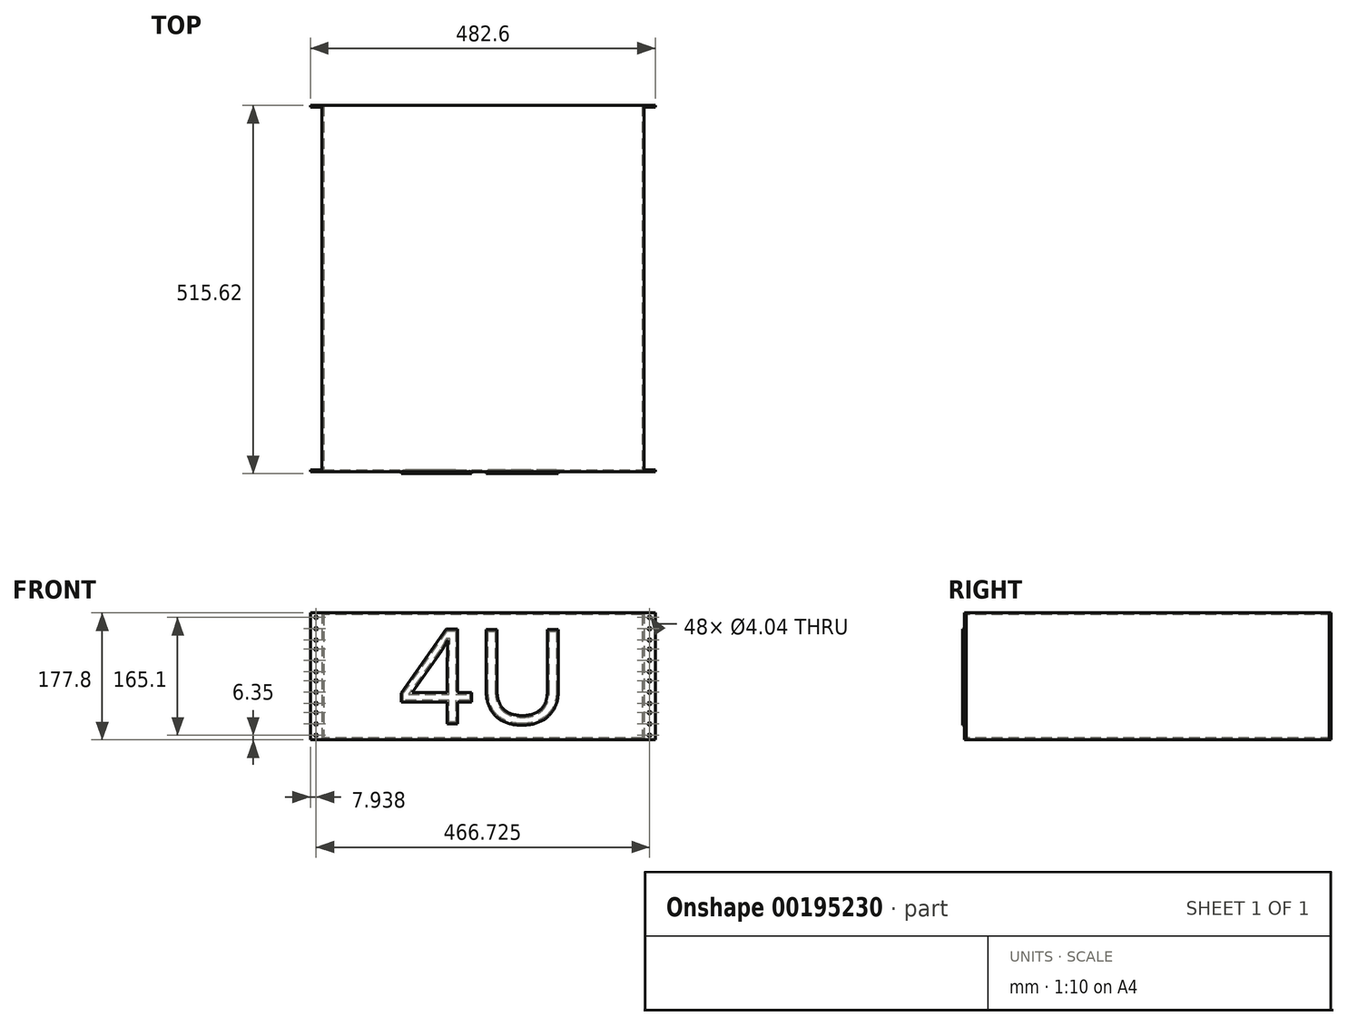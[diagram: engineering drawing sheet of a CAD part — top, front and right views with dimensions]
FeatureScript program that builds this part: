
annotation { "Feature Type Name" : "Feature", "Feature Type Description" : "" }
export const myFeature = defineFeature(function(context is Context, id is Id, definition is map)
    precondition{}
    {
        {
            var Q0;
            Q0=qCreatedBy(makeId("Front.planeOp"),FACE);
            var sketch = newSketch(context, id + "F0", { "sketchPlane" : qUnion([Q0])});
            skLineSegment(sketch, "E0.bottom", {"start": v(-241.3, 88.9) * mm, "end": v(241.3, 88.9) * mm});
            skLineSegment(sketch, "E0.top", {"start": v(-241.3, -88.9) * mm, "end": v(241.3, -88.9) * mm});
            skLineSegment(sketch, "E0.left", {"start": v(-241.3, 88.9) * mm, "end": v(-241.3, -88.9) * mm});
            skLineSegment(sketch, "E0.right", {"start": v(241.3, 88.9) * mm, "end": v(241.3, -88.9) * mm});
            skPoint(sketch, "E0.middle", {"position": v(0, 0) * mm});
            skSolve(sketch);
        }
        {
            var Q0;
            Q0 = qSketchRegion(id + "F0", true);
            extrude(context, id + "F1", {"entities" : qUnion([Q0]), "depth" : 2.54 * mm});
        }
        {
            var Q0;
            Q0=makeQuery(id+"F1.opExtrude","CAP_FACE",FACE,{"disambiguationData":[OSD([sQuery(id+"F0.wireOp",EDGE,"E0.bottom"),sQuery(id+"F0.wireOp",EDGE,"E0.top"),sQuery(id+"F0.wireOp",EDGE,"E0.left"),sQuery(id+"F0.wireOp",EDGE,"E0.right")])],"isStart":true});
            var sketch = newSketch(context, id + "F2", { "sketchPlane" : qUnion([Q0])});
            skLineSegment(sketch, "E1.bottom", {"start": v(-225.42, 88.9) * mm, "end": v(225.42, 88.9) * mm});
            skLineSegment(sketch, "E1.top", {"start": v(-225.42, -88.9) * mm, "end": v(225.42, -88.9) * mm});
            skLineSegment(sketch, "E1.left", {"start": v(-225.42, 88.9) * mm, "end": v(-225.42, -88.9) * mm});
            skLineSegment(sketch, "E1.right", {"start": v(225.42, 88.9) * mm, "end": v(225.42, -88.9) * mm});
            skPoint(sketch, "E1.middle", {"position": v(0, 0) * mm});
            skSolve(sketch);
        }
        {
            var Q0;
            Q0 = qSketchRegion(id + "F2", true);
            extrude(context, id + "F3", {"entities" : qUnion([Q0]), "operationType" : NewBodyOperationType.ADD, "depth" : 508 * mm});
        }
        {
            var Q0;
            Q0=makeQuery(id+"F3.opExtrude","CAP_FACE",FACE,{"disambiguationData":[OSD([sQuery(id+"F2.wireOp",EDGE,"E1.bottom"),sQuery(id+"F2.wireOp",EDGE,"E1.top"),sQuery(id+"F2.wireOp",EDGE,"E1.left"),sQuery(id+"F2.wireOp",EDGE,"E1.right")])],"isStart":false});
            var sketch = newSketch(context, id + "F4", { "sketchPlane" : qUnion([Q0])});
            skLineSegment(sketch, "E2.bottom", {"start": v(-241.3, 88.9) * mm, "end": v(241.3, 88.9) * mm});
            skLineSegment(sketch, "E2.top", {"start": v(-241.3, -88.9) * mm, "end": v(241.3, -88.9) * mm});
            skLineSegment(sketch, "E2.left", {"start": v(-241.3, 88.9) * mm, "end": v(-241.3, -88.9) * mm});
            skLineSegment(sketch, "E2.right", {"start": v(241.3, 88.9) * mm, "end": v(241.3, -88.9) * mm});
            skPoint(sketch, "E2.middle", {"position": v(0, 0) * mm});
            skSolve(sketch);
        }
        {
            var Q0;
            Q0 = qSketchRegion(id + "F4", true);
            extrude(context, id + "F5", {"entities" : qUnion([Q0]), "operationType" : NewBodyOperationType.ADD, "depth" : 2.54 * mm});
        }
        {
            var Q0;
            Q0=makeQuery(id+"F1.opExtrude","CAP_FACE",FACE,{"disambiguationData":[OSD([sQuery(id+"F0.wireOp",EDGE,"E0.bottom"),sQuery(id+"F0.wireOp",EDGE,"E0.top"),sQuery(id+"F0.wireOp",EDGE,"E0.left"),sQuery(id+"F0.wireOp",EDGE,"E0.right")])],"isStart":false});
            var sketch = newSketch(context, id + "F6", { "sketchPlane" : qUnion([Q0])});
            skPoint(sketch, "E3", {"position": v(-233.36, 82.55) * mm});
            skPoint(sketch, "E4", {"position": v(-233.36, 66.68) * mm});
            skPoint(sketch, "E5", {"position": v(-233.36, 50.8) * mm});
            skPoint(sketch, "E6.0.1.0", {"position": v(-233.36, 38.1) * mm});
            skPoint(sketch, "E6.0.1.1", {"position": v(-233.36, 22.23) * mm});
            skPoint(sketch, "E6.0.1.2", {"position": v(-233.36, 6.35) * mm});
            skPoint(sketch, "E6.0.2.0", {"position": v(-233.36, -6.35) * mm});
            skPoint(sketch, "E6.0.2.1", {"position": v(-233.36, -22.22) * mm});
            skPoint(sketch, "E6.0.2.2", {"position": v(-233.36, -38.1) * mm});
            skPoint(sketch, "E6.0.3.0", {"position": v(-233.36, -50.8) * mm});
            skPoint(sketch, "E6.0.3.1", {"position": v(-233.36, -66.67) * mm});
            skPoint(sketch, "E6.0.3.2", {"position": v(-233.36, -82.55) * mm});
            skPoint(sketch, "E6.1.0.0", {"position": v(233.36, 82.55) * mm});
            skPoint(sketch, "E6.1.0.1", {"position": v(233.36, 66.68) * mm});
            skPoint(sketch, "E6.1.0.2", {"position": v(233.36, 50.8) * mm});
            skPoint(sketch, "E6.1.1.0", {"position": v(233.36, 38.1) * mm});
            skPoint(sketch, "E6.1.1.1", {"position": v(233.36, 22.23) * mm});
            skPoint(sketch, "E6.1.1.2", {"position": v(233.36, 6.35) * mm});
            skPoint(sketch, "E6.1.2.0", {"position": v(233.36, -6.35) * mm});
            skPoint(sketch, "E6.1.2.1", {"position": v(233.36, -22.22) * mm});
            skPoint(sketch, "E6.1.2.2", {"position": v(233.36, -38.1) * mm});
            skPoint(sketch, "E6.1.3.0", {"position": v(233.36, -50.8) * mm});
            skPoint(sketch, "E6.1.3.1", {"position": v(233.36, -66.67) * mm});
            skPoint(sketch, "E6.1.3.2", {"position": v(233.36, -82.55) * mm});
            skLineSegment(sketch, "E6.direction1", {"start": v(-233.36, 82.55) * mm, "end": v(233.36, 82.55) * mm, "construction": true});
            skLineSegment(sketch, "E6.direction2", {"start": v(-233.36, 82.55) * mm, "end": v(-233.36, 38.1) * mm, "construction": true});
            skSolve(sketch);
        }
        {
            var Q0;
            Q0=sQuery(id+"F6.wireOp",VERTEX,"E6.1.2.1");
            var Q1;
            Q1=sQuery(id+"F6.wireOp",VERTEX,"E6.0.1.1");
            var Q2;
            Q2=sQuery(id+"F6.wireOp",VERTEX,"E6.1.2.2");
            var Q3;
            Q3=sQuery(id+"F6.wireOp",VERTEX,"E6.0.1.2");
            var Q4;
            Q4=sQuery(id+"F6.wireOp",VERTEX,"E6.0.2.0");
            var Q5;
            Q5=sQuery(id+"F6.wireOp",VERTEX,"E6.0.2.1");
            var Q6;
            Q6=sQuery(id+"F6.wireOp",VERTEX,"E6.0.2.2");
            var Q7;
            Q7=sQuery(id+"F6.wireOp",VERTEX,"E6.1.0.1");
            var Q8;
            Q8=sQuery(id+"F6.wireOp",VERTEX,"E6.1.0.0");
            var Q9;
            Q9=sQuery(id+"F6.wireOp",VERTEX,"E6.1.3.2");
            var Q10;
            Q10=sQuery(id+"F6.wireOp",VERTEX,"E6.1.3.1");
            var Q11;
            Q11=sQuery(id+"F6.wireOp",VERTEX,"E6.1.3.0");
            var Q12;
            Q12=sQuery(id+"F6.wireOp",VERTEX,"E6.0.3.0");
            var Q13;
            Q13=sQuery(id+"F6.wireOp",VERTEX,"E6.0.3.1");
            var Q14;
            Q14=sQuery(id+"F6.wireOp",VERTEX,"E6.1.2.0");
            var Q15;
            Q15=sQuery(id+"F6.wireOp",VERTEX,"E6.0.3.2");
            var Q16;
            Q16=sQuery(id+"F6.wireOp",VERTEX,"E6.1.1.2");
            var Q17;
            Q17=sQuery(id+"F6.wireOp",VERTEX,"E6.1.1.1");
            var Q18;
            Q18=sQuery(id+"F6.wireOp",VERTEX,"E6.1.1.0");
            var Q19;
            Q19=sQuery(id+"F6.wireOp",VERTEX,"E6.1.0.2");
            var Q20;
            Q20=sQuery(id+"F6.wireOp",VERTEX,"E3");
            var Q21;
            Q21=sQuery(id+"F6.wireOp",VERTEX,"E4");
            var Q22;
            Q22=sQuery(id+"F6.wireOp",VERTEX,"E5");
            var Q23;
            Q23=sQuery(id+"F6.wireOp",VERTEX,"E6.0.1.0");
            var Q24;
            Q24=makeQuery(id+"F1.opExtrude","SWEPT_BODY",BODY,{"disambiguationData":[OSD([sQuery(id+"F0.wireOp",EDGE,"E0.bottom"),sQuery(id+"F0.wireOp",EDGE,"E0.top"),sQuery(id+"F0.wireOp",EDGE,"E0.left"),sQuery(id+"F0.wireOp",EDGE,"E0.right")])]});
            hole(context, id + "F7", {"style" : HoleStyle.SIMPLE, "endStyle" : HoleEndStyle.THROUGH, "standardTappedOrClearance" : lookupTablePath({ "standard" : "ANSI", "engagement" : "75%", "pitch" : "32 tpi", "size" : "#10", "type" : "Tapped" }), "standardBlindInLast" : lookupTablePath({ "standard" : "ANSI", "engagement" : "75%", "pitch" : "32 tpi", "size" : "#10", "type" : "Tapped" }), "holeDiameter" : 4.04 * mm, "locations" : qUnion([Q0, Q1, Q2, Q3, Q4, Q5, Q6, Q7, Q8, Q9, Q10, Q11, Q12, Q13, Q14, Q15, Q16, Q17, Q18, Q19, Q20, Q21, Q22, Q23]), "scope" : qUnion([Q24]), "isTappedThrough" : true, "majorDiameter" : 4.83 * mm, "showTappedDepth" : true});
        }
        {
            var Q0;
            Q0=makeQuery(id+"F1.opExtrude","CAP_FACE",FACE,{"disambiguationData":[OSD([sQuery(id+"F0.wireOp",EDGE,"E0.bottom"),sQuery(id+"F0.wireOp",EDGE,"E0.top"),sQuery(id+"F0.wireOp",EDGE,"E0.left"),sQuery(id+"F0.wireOp",EDGE,"E0.right")])],"isStart":false});
            var sketch = newSketch(context, id + "F8", { "sketchPlane" : qUnion([Q0])});
            skText(sketch, "E7", { "text": "4U\n", "fontName": "OpenSans-Regular.ttf"});
            const initialGuessF8  = {"E7": [-0.11768, -0.06652, 1, 0, 0.13304]};
            skSetInitialGuess(sketch, initialGuessF8);
            skSolve(sketch);
        }
        {
            var Q0;
            Q0 = qSketchRegion(id + "F8", true);
            extrude(context, id + "F9", {"entities" : qUnion([Q0]), "operationType" : NewBodyOperationType.ADD, "depth" : 2.54 * mm});
        }
        {
            var Q0;
            Q0=makeQuery(id+"F5.opExtrude","CAP_FACE",FACE,{"disambiguationData":[OSD([sQuery(id+"F4.wireOp",EDGE,"E2.bottom"),sQuery(id+"F4.wireOp",EDGE,"E2.top"),sQuery(id+"F4.wireOp",EDGE,"E2.left"),sQuery(id+"F4.wireOp",EDGE,"E2.right")])],"isStart":false});
            shell(context, id + "F10", {"entities" : qUnion([Q0]), "thickness" : 2.54 * mm});
        }
    });
